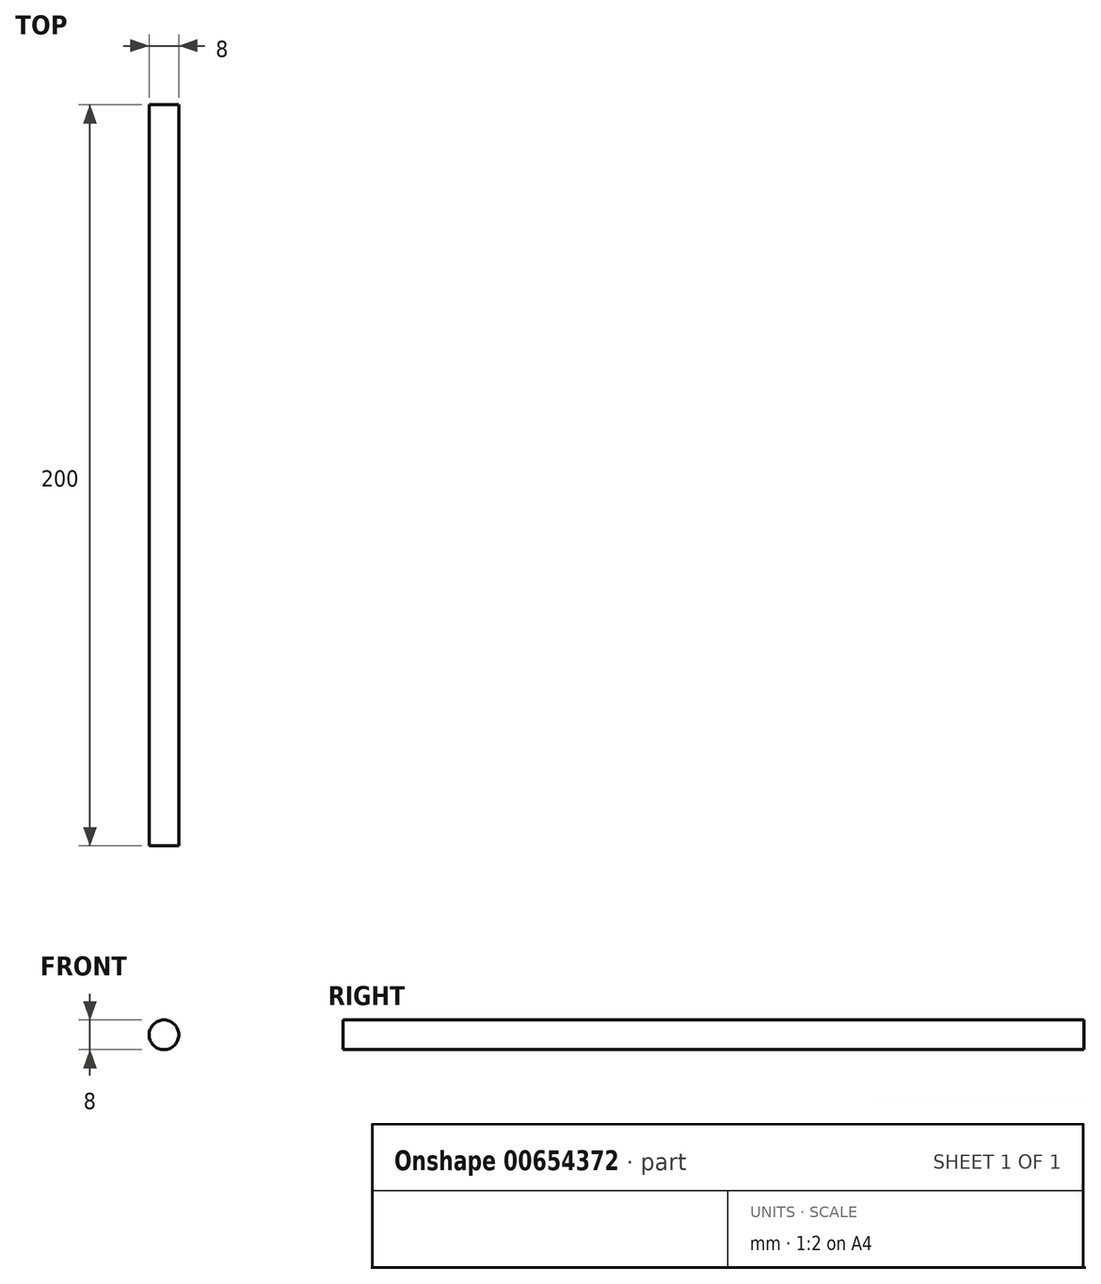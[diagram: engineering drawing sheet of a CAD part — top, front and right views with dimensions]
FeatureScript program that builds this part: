
annotation { "Feature Type Name" : "Feature", "Feature Type Description" : "" }
export const myFeature = defineFeature(function(context is Context, id is Id, definition is map)
    precondition{}
    {
        {
            assignVariable(context, id + "F0", {"name" : "lunghezza_barra", "anyValue" : 200 * mm});
        }
        {
            var Q0;
            Q0=qCreatedBy(makeId("Front.planeOp"),FACE);
            var sketch = newSketch(context, id + "F1", { "sketchPlane" : qUnion([Q0])});
            skCircle(sketch, "E0", {"center": v(0, 0) * mm, "radius": 4 * mm});
            skSolve(sketch);
        }
        {
            var Q0;
            Q0=makeQuery(id+"F1.imprint","IMPRINT",FACE,{"disambiguationData":[TD([[makeQuery(id+"F1.imprint","IMPRINT",EDGE,{"derivedFrom":sQuery(id+"F1.wireOp",EDGE,"E0")}),1.0]])]});
            extrude(context, id + "F2", {"entities" : qUnion([Q0]), "oppositeDirection" : true, "depth" : getVariable(context, 'lunghezza_barra'), "offsetDistance" : 25 * mm});
        }
    });
